# Revit family: TR2040_C
name_source: partatom
category: Verbindungsmittel
units: mm (PartAtom-declared; Revit-internal decimal feet)

## family parameters
Arbeitsebenenbasiert = Nein
Beim Laden mit Abzugskörper schneiden = Nein
Gemeinsam genutzt = Nein
Immer vertikal = Nein
OmniClass-Nummer = 23.25.10.27.11.21
OmniClass-Titel = Reinforcement Couplers

## types (10) — shared parameters
Endenbearbeitung 1 = Mit Gewinde
Endenbearbeitung 2 = Mit Gewinde
Hersteller = Stahlwerk Annahütte Max Aicher GmbH Co.KG
Modell = TR 2040C
Stabgröße 2 = Keine
TR2040C-G_Vis = Ja
TR2040C-L_Vis = Ja
TR2040C-SW_Vis = Ja
Typenbild = TR2040C.png
URL = http//:www.annahuette.com
zero-valued in all types: Einfassung Stab 2

## per-type parameters (varying)
| type | Außendurchmesser | Beschreibung | Einfassung Stab 1 | Gesamtlänge | Körper | Stabgröße 1 | TR2040C-G | TR2040C-L | TR2040C-Lsw | TR2040C-SW | TR2040C-ø | TR2040C-ød | Typenkommentare |
| TR 2040C-ø18 | 30 mm  [stored 0.0984252 ft] | TR2040C-ø18 | 16 mm  [stored 0.0524934 ft] | 22 mm  [stored 0.0721785 ft] | 0,10 kg | SAS 670 - ø18 | 0,10 kg | 22 mm  [stored 0.0721785 ft] | 16 mm  [stored 0.0524934 ft] | 30 mm  [stored 0.0984252 ft] | 35 mm  [stored 0.114829 ft] | 18 mm  [stored 0.0590551 ft] | TR 2040C- Kontermutter, kurz Gus |
| TR 2040C-ø22 | 36 mm  [stored 0.11811 ft] | TR2040C-ø22 | 16 mm  [stored 0.0524934 ft] | 22 mm  [stored 0.0721785 ft] | 0,12 kg | SAS 670 - ø22 | 0,12 kg | 22 mm  [stored 0.0721785 ft] | 16 mm  [stored 0.0524934 ft] | 36 mm  [stored 0.11811 ft] | 42 mm  [stored 0.137795 ft] | 22 mm  [stored 0.0721785 ft] | TR 2040C - Kontermutter, kurz Guss |
| TR 2040C-ø25 | 41 mm  [stored 0.134514 ft] | TR2040C-ø25 | 16 mm  [stored 0.0524934 ft] | 22 mm  [stored 0.0721785 ft] | 0,16 kg | SAS 670 - ø25 | 0,16 kg | 22 mm  [stored 0.0721785 ft] | 16 mm  [stored 0.0524934 ft] | 41 mm  [stored 0.134514 ft] | 47 mm  [stored 0.154199 ft] | 25 mm  [stored 0.082021 ft] | TR 2040C - Kontermutter, kurz Guss |
| TR 2040C-ø28 | 46 mm  [stored 0.150919 ft] | TR2040C-ø28 | 24 mm  [stored 0.0787402 ft] | 30 mm  [stored 0.0984252 ft] | 0,26 kg | SAS 670 - ø28 | 0,26 kg | 30 mm  [stored 0.0984252 ft] | 24 mm  [stored 0.0787402 ft] | 46 mm  [stored 0.150919 ft] | 53 mm  [stored 0.173885 ft] | 28 mm  [stored 0.0918635 ft] | TR 2040C - Kontermutter, kurz Guss |
| TR 2040C-ø30 | 50 mm  [stored 0.164042 ft] | TR2040C-ø30 | 24 mm  [stored 0.0787402 ft] | 30 mm  [stored 0.0984252 ft] | 0,31 kg | SAS 670 - ø30 | 0,31 kg | 30 mm  [stored 0.0984252 ft] | 24 mm  [stored 0.0787402 ft] | 50 mm  [stored 0.164042 ft] | 58 mm  [stored 0.190289 ft] | 30 mm  [stored 0.0984252 ft] | TR 2040C -Kontermutter, kurz Guss |
| TR 2040C-ø35 | 55 mm  [stored 0.180446 ft] | TR2040C-ø35 | 32 mm  [stored 0.104987 ft] | 40 mm  [stored 0.131234 ft] | 0,47 kg | SAS 670 - ø35 | 0,47 kg | 40 mm  [stored 0.131234 ft] | 32 mm  [stored 0.104987 ft] | 55 mm  [stored 0.180446 ft] | 64 mm  [stored 0.209974 ft] | 35 mm  [stored 0.114829 ft] | TR 2040C - Kontermutter, kurz Guss |
| TR 2040C-ø43 | 70 mm  [stored 0.229659 ft] | TR2040C-ø43 | 40 mm  [stored 0.131234 ft] | 50 mm  [stored 0.164042 ft] | 1,00 kg | SAS 670 - ø43 | 1,00 kg | 50 mm  [stored 0.164042 ft] | 40 mm  [stored 0.131234 ft] | 70 mm  [stored 0.229659 ft] | 81 mm  [stored 0.265748 ft] | 43 mm  [stored 0.141076 ft] | TR 2040C - Kontermutter, kurz Guss |
| TR 2040C-ø50 | 80 mm  [stored 0.262467 ft] | TR2040C-ø50 | 40 mm  [stored 0.131234 ft] | 50 mm  [stored 0.164042 ft] | 1,26 kg | SAS 670 - ø50 | 1,26 kg | 50 mm  [stored 0.164042 ft] | 40 mm  [stored 0.131234 ft] | 80 mm  [stored 0.262467 ft] | 90 mm  [stored 0.295276 ft] | 50 mm  [stored 0.164042 ft] | TR 2040C - Kontermutter, kurz Guss |
| TR 2040C-ø57,5 | 90 mm  [stored 0.295276 ft] | TR2040C-ø57,5 | 50 mm  [stored 0.164042 ft] | 60 mm  [stored 0.19685 ft] | 2,04 kg | SAS 670 - ø57,5 | 2,04 kg | 60 mm  [stored 0.19685 ft] | 50 mm  [stored 0.164042 ft] | 90 mm  [stored 0.295276 ft] | 102 mm | 58 mm  [stored 0.190289 ft] | TR 2040C - Kontermutter, kurz Guss |
| TR 2040C-ø63,5 | 100 mm  [stored 0.328084 ft] | TR2040C-ø63,5 | 50 mm  [stored 0.164042 ft] | 70 mm  [stored 0.229659 ft] | 2,70 kg | SAS 670 - ø63,5 | 2,70 kg | 70 mm  [stored 0.229659 ft] | 50 mm  [stored 0.164042 ft] | 100 mm  [stored 0.328084 ft] | 114 mm  [stored 0.374016 ft] | 64 mm  [stored 0.209974 ft] | TR 2040C - Kontermutter, kurz Guss |

note: [stored X ft] marks values corroborated as IEEE doubles in the binary element streams (Revit-internal decimal feet)
